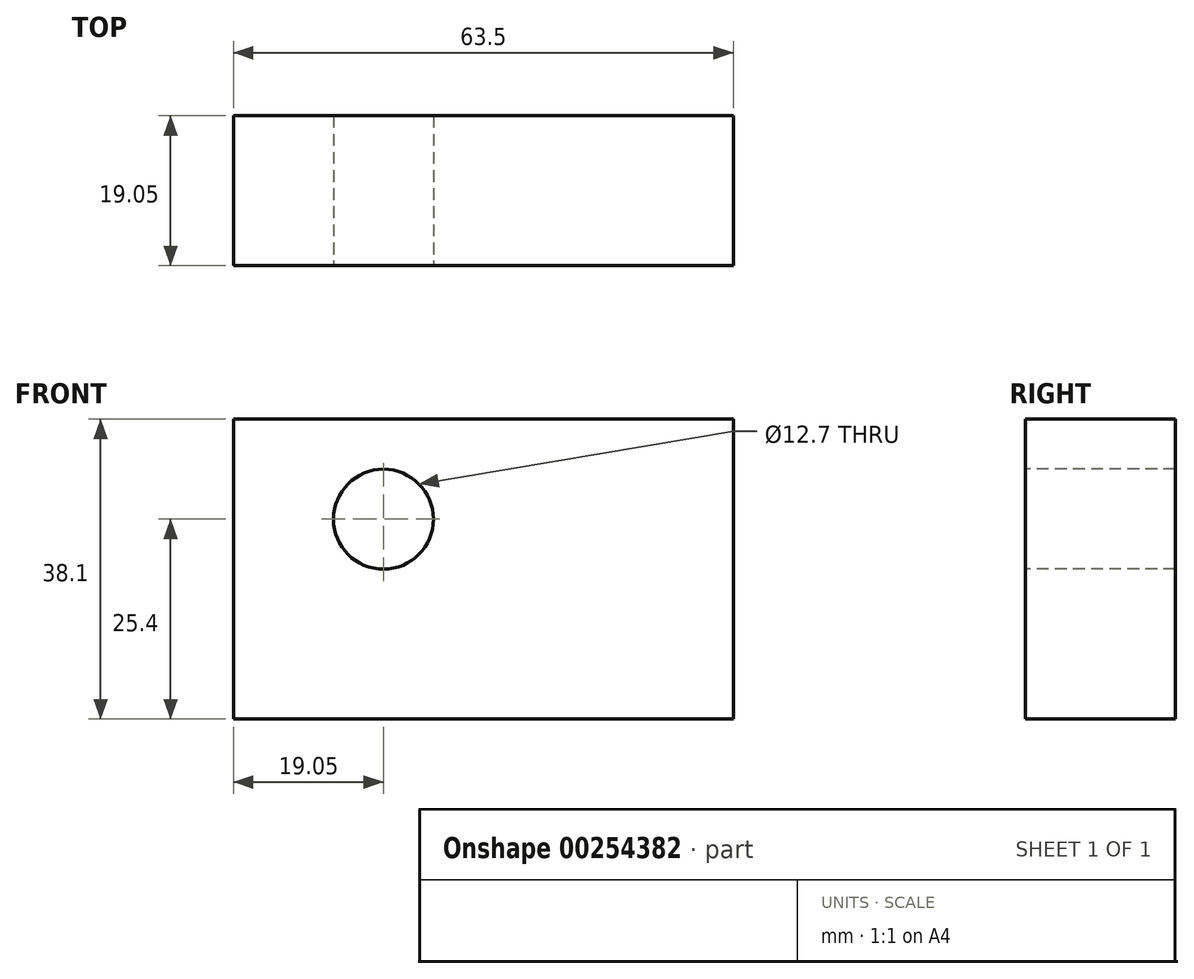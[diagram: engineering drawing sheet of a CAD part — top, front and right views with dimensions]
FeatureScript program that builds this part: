
annotation { "Feature Type Name" : "Feature", "Feature Type Description" : "" }
export const myFeature = defineFeature(function(context is Context, id is Id, definition is map)
    precondition{}
    {
        {
            var Q0;
            Q0=qCreatedBy(makeId("Front.planeOp"),FACE);
            var sketch = newSketch(context, id + "F0", { "sketchPlane" : qUnion([Q0])});
            skLineSegment(sketch, "E0.bottom", {"start": v(0, 0) * mm, "end": v(63.5, 0) * mm});
            skLineSegment(sketch, "E0.top", {"start": v(0, 38.1) * mm, "end": v(63.5, 38.1) * mm});
            skLineSegment(sketch, "E0.left", {"start": v(0, 0) * mm, "end": v(0, 38.1) * mm});
            skLineSegment(sketch, "E0.right", {"start": v(63.5, 0) * mm, "end": v(63.5, 38.1) * mm});
            skSolve(sketch);
        }
        {
            var Q0;
            Q0=makeQuery(id+"F0.imprint","IMPRINT",FACE,{"disambiguationData":[TD([[makeQuery(id+"F0.imprint","IMPRINT",EDGE,{"derivedFrom":sQuery(id+"F0.wireOp",EDGE,"E0.bottom")}),1.0]])]});
            extrude(context, id + "F1", {"entities" : qUnion([Q0]), "depth" : 19.05 * mm});
        }
        {
            var Q0;
            Q0=makeQuery(id+"F1.opExtrude","CAP_FACE",FACE,{"disambiguationData":[OSD([sQuery(id+"F0.wireOp",EDGE,"E0.bottom"),sQuery(id+"F0.wireOp",EDGE,"E0.top"),sQuery(id+"F0.wireOp",EDGE,"E0.left"),sQuery(id+"F0.wireOp",EDGE,"E0.right")])],"isStart":false});
            var sketch = newSketch(context, id + "F2", { "sketchPlane" : qUnion([Q0])});
            skCircle(sketch, "E1", {"center": v(19.05, 25.4) * mm, "radius": 6.35 * mm});
            skSolve(sketch);
        }
        {
            var Q0;
            Q0=sQuery(id+"F2.wireOp",VERTEX,"E1.center");
            var Q1;
            Q1=makeQuery(id+"F1.opExtrude","SWEPT_BODY",BODY,{"disambiguationData":[OSD([sQuery(id+"F0.wireOp",EDGE,"E0.bottom"),sQuery(id+"F0.wireOp",EDGE,"E0.top"),sQuery(id+"F0.wireOp",EDGE,"E0.left"),sQuery(id+"F0.wireOp",EDGE,"E0.right")])]});
            hole(context, id + "F3", {"style" : HoleStyle.SIMPLE, "endStyle" : HoleEndStyle.THROUGH, "holeDiameter" : 12.7 * mm, "tappedDepth" : 12.7 * mm, "tapClearance" : 3, "locations" : qUnion([Q0]), "scope" : qUnion([Q1])});
        }
    });
